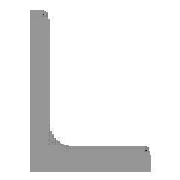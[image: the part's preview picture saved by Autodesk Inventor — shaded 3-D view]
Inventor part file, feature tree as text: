
AUTODESK INVENTOR PART (.ipt)
format: ipt  version: 2024.1 (Build 281209000, 209)  size: 120,832 bytes
history: native  units: mm (DEFAULTED — no unit token found)
features: other x4, sketch x1, plane x1
ambient origin geometry x8: Origin, YZ Plane, XZ Plane, XY Plane, X Axis, Y Axis, Z Axis, Center Point
bodies: Solid1 (feature_tree), Body (feature_tree)
feature tree (6):
  parser-record x1  (decoder bookkeeping rows leaked as tree rows — omitted from the tree; the rows remain in map.json)
  other  "Driven Length"
  other  "Start Plane"
  other  "End Plane"
  sketch  "Sketch3"  dims[d0=28.702mm d1=28.702mm d2=3.175mm d3=3.175mm d4=1000.0mm d5=0.0mm d10=0.0mm d11=0.0mm d12=-0.0mm d13=1000.0mm d14=2.286mm d15=1.27mm d16=90.0deg d17=1000.0mm]
  plane  "Work Plane3"
